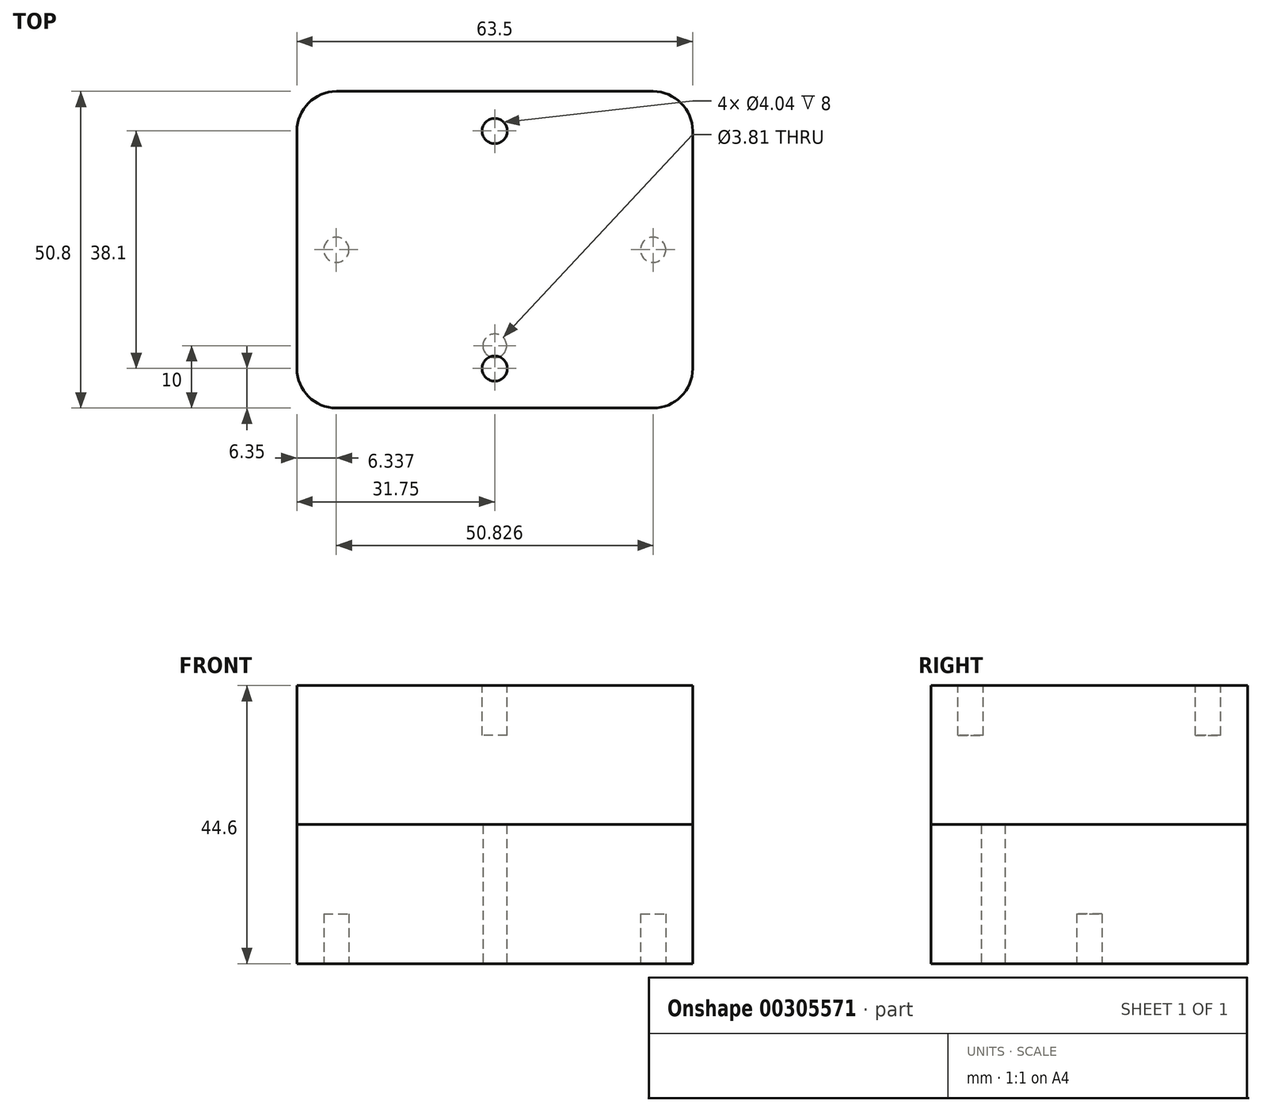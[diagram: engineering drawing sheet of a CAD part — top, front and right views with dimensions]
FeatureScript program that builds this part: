
annotation { "Feature Type Name" : "Feature", "Feature Type Description" : "" }
export const myFeature = defineFeature(function(context is Context, id is Id, definition is map)
    precondition{}
    {
        {
            var Q0;
            Q0=qCreatedBy(makeId("Top.planeOp"),FACE);
            var sketch = newSketch(context, id + "F0", { "sketchPlane" : qUnion([Q0])});
            skLineSegment(sketch, "E0.bottom", {"start": v(25.4, 25.4) * mm, "end": v(-25.4, 25.4) * mm});
            skLineSegment(sketch, "E0.top", {"start": v(25.4, -25.4) * mm, "end": v(-25.4, -25.4) * mm});
            skLineSegment(sketch, "E0.left", {"start": v(31.75, 19.05) * mm, "end": v(31.75, -19.05) * mm});
            skLineSegment(sketch, "E0.right", {"start": v(-31.75, 19.05) * mm, "end": v(-31.75, -19.05) * mm});
            skPoint(sketch, "E0.middle", {"position": v(0, 0) * mm});
            skPoint(sketch, "E1.visualSharp", {"position": v(-31.75, 25.4) * mm});
            skArc(sketch, "E1.filletArc", {"start": v(-25.4, 25.4) * mm, "mid": v(-29.9, 23.54) * mm, "end": v(-31.75, 19.05) * mm});
            skPoint(sketch, "E2.visualSharp", {"position": v(31.75, 25.4) * mm});
            skArc(sketch, "E2.filletArc", {"start": v(31.75, 19.05) * mm, "mid": v(29.9, 23.54) * mm, "end": v(25.4, 25.4) * mm});
            skPoint(sketch, "E3.visualSharp", {"position": v(31.75, -25.4) * mm});
            skArc(sketch, "E3.filletArc", {"start": v(25.4, -25.4) * mm, "mid": v(29.9, -23.54) * mm, "end": v(31.75, -19.05) * mm});
            skPoint(sketch, "E4.visualSharp", {"position": v(-31.75, -25.4) * mm});
            skArc(sketch, "E4.filletArc", {"start": v(-31.75, -19.05) * mm, "mid": v(-29.9, -23.54) * mm, "end": v(-25.4, -25.4) * mm});
            skSolve(sketch);
        }
        {
            var Q0;
            Q0 = qSketchRegion(id + "F0", true);
            extrude(context, id + "F1", {"entities" : qUnion([Q0]), "depth" : 22.3 * mm});
        }
        {
            var Q0;
            Q0=makeQuery(id+"F1.opExtrude","CAP_FACE",FACE,{"disambiguationData":[OSD([sQuery(id+"F0.wireOp",EDGE,"E0.bottom"),sQuery(id+"F0.wireOp",EDGE,"E0.top"),sQuery(id+"F0.wireOp",EDGE,"E0.left"),sQuery(id+"F0.wireOp",EDGE,"E0.right"),sQuery(id+"F0.wireOp",EDGE,"E1.filletArc"),sQuery(id+"F0.wireOp",EDGE,"E2.filletArc"),sQuery(id+"F0.wireOp",EDGE,"E3.filletArc"),sQuery(id+"F0.wireOp",EDGE,"E4.filletArc")])],"isStart":false});
            var sketch = newSketch(context, id + "F2", { "sketchPlane" : qUnion([Q0])});
            skCircle(sketch, "E5", {"center": v(0, 19.05) * mm, "radius": 2.02 * mm});
            skCircle(sketch, "E6.MirrorC", {"center": v(0, -19.05) * mm, "radius": 2.02 * mm});
            skSolve(sketch);
        }
        {
            var Q0;
            Q0 = qSketchRegion(id + "F2", true);
            extrude(context, id + "F3", {"entities" : qUnion([Q0]), "operationType" : NewBodyOperationType.REMOVE, "oppositeDirection" : true, "depth" : 8 * mm});
        }
        {
            var Q0;
            Q0=makeQuery(id+"F1.opExtrude","CAP_FACE",FACE,{"disambiguationData":[OSD([sQuery(id+"F0.wireOp",EDGE,"E0.bottom"),sQuery(id+"F0.wireOp",EDGE,"E0.top"),sQuery(id+"F0.wireOp",EDGE,"E0.left"),sQuery(id+"F0.wireOp",EDGE,"E0.right"),sQuery(id+"F0.wireOp",EDGE,"E1.filletArc"),sQuery(id+"F0.wireOp",EDGE,"E2.filletArc"),sQuery(id+"F0.wireOp",EDGE,"E3.filletArc"),sQuery(id+"F0.wireOp",EDGE,"E4.filletArc")])],"isStart":true});
            extrude(context, id + "F4", {"entities" : qUnion([Q0]), "depth" : 22.3 * mm});
        }
        {
            var Q0;
            Q0=makeQuery(id+"F4.opExtrude","CAP_FACE",FACE,{"disambiguationData":[OSD([sQuery(id+"F0.wireOp",EDGE,"E0.bottom"),sQuery(id+"F0.wireOp",EDGE,"E0.top"),sQuery(id+"F0.wireOp",EDGE,"E0.left"),sQuery(id+"F0.wireOp",EDGE,"E0.right"),sQuery(id+"F0.wireOp",EDGE,"E1.filletArc"),sQuery(id+"F0.wireOp",EDGE,"E2.filletArc"),sQuery(id+"F0.wireOp",EDGE,"E3.filletArc"),sQuery(id+"F0.wireOp",EDGE,"E4.filletArc")])],"isStart":false});
            var sketch = newSketch(context, id + "F5", { "sketchPlane" : qUnion([Q0])});
            skCircle(sketch, "E7", {"center": v(0, 15.4) * mm, "radius": 1.9 * mm});
            skSolve(sketch);
        }
        {
            var Q0;
            Q0 = qSketchRegion(id + "F5", true);
            extrude(context, id + "F6", {"entities" : qUnion([Q0]), "operationType" : NewBodyOperationType.REMOVE, "endBound" : BoundingType.UP_TO_NEXT, "oppositeDirection" : true, "depth" : 25 * mm});
        }
        {
            var Q0;
            Q0=makeQuery(id+"F4.opExtrude","CAP_FACE",FACE,{"disambiguationData":[OSD([sQuery(id+"F0.wireOp",EDGE,"E0.bottom"),sQuery(id+"F0.wireOp",EDGE,"E0.top"),sQuery(id+"F0.wireOp",EDGE,"E0.left"),sQuery(id+"F0.wireOp",EDGE,"E0.right"),sQuery(id+"F0.wireOp",EDGE,"E1.filletArc"),sQuery(id+"F0.wireOp",EDGE,"E2.filletArc"),sQuery(id+"F0.wireOp",EDGE,"E3.filletArc"),sQuery(id+"F0.wireOp",EDGE,"E4.filletArc")])],"isStart":false});
            var sketch = newSketch(context, id + "F7", { "sketchPlane" : qUnion([Q0])});
            skCircle(sketch, "E8", {"center": v(-25.41, 0) * mm, "radius": 2.02 * mm});
            skCircle(sketch, "E9.MirrorC", {"center": v(25.41, 0) * mm, "radius": 2.02 * mm});
            skSolve(sketch);
        }
        {
            var Q0;
            Q0 = qSketchRegion(id + "F7", true);
            extrude(context, id + "F8", {"entities" : qUnion([Q0]), "operationType" : NewBodyOperationType.REMOVE, "oppositeDirection" : true, "depth" : 8 * mm});
        }
    });
